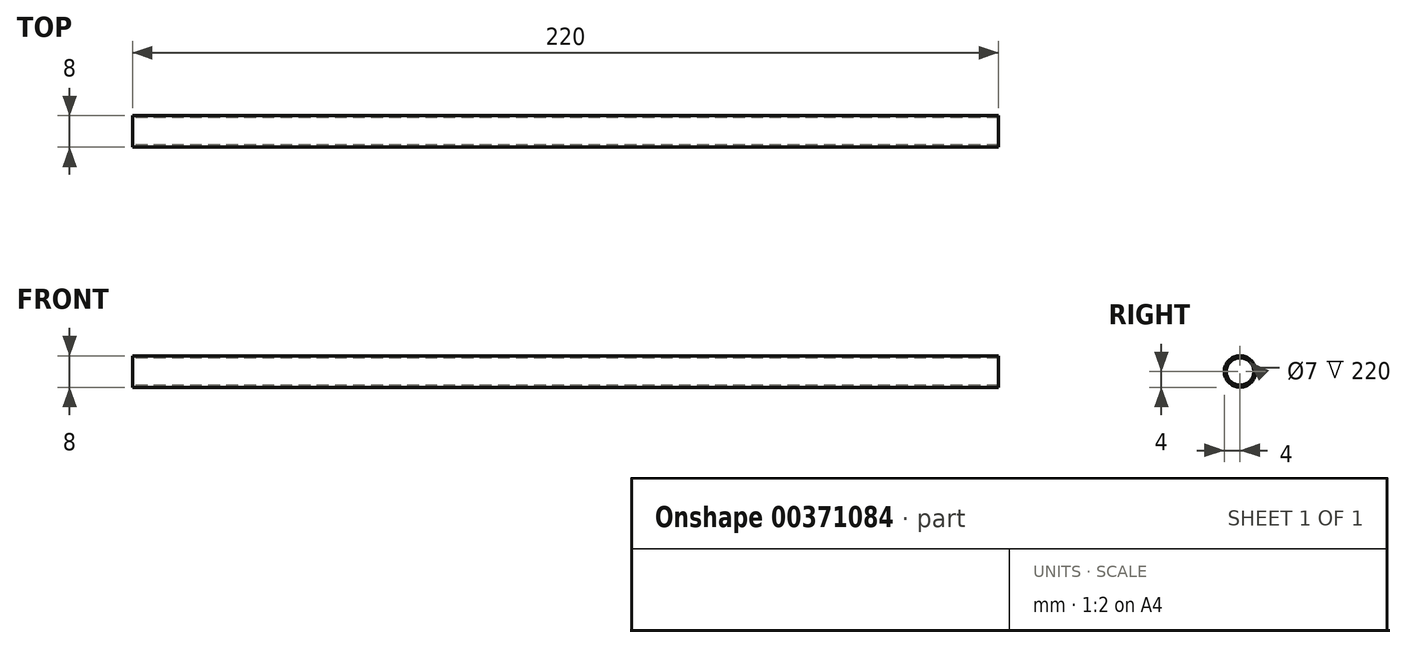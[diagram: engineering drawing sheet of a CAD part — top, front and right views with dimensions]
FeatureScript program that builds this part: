
annotation { "Feature Type Name" : "Feature", "Feature Type Description" : "" }
export const myFeature = defineFeature(function(context is Context, id is Id, definition is map)
    precondition{}
    {
        {
            var Q0;
            Q0=qCreatedBy(makeId("Right.planeOp"),FACE);
            var sketch = newSketch(context, id + "F0", { "sketchPlane" : qUnion([Q0])});
            skCircle(sketch, "E0", {"center": v(0, 0) * mm, "radius": 4 * mm});
            skCircle(sketch, "E1", {"center": v(0, 0) * mm, "radius": 3.5 * mm});
            skSolve(sketch);
        }
        {
            var Q0;
            Q0=makeQuery(id+"F0.imprint","IMPRINT",FACE,{"disambiguationData":[TD([[makeQuery(id+"F0.imprint","IMPRINT",EDGE,{"derivedFrom":sQuery(id+"F0.wireOp",EDGE,"E0")}),1.0]])]});
            extrude(context, id + "F1", {"entities" : qUnion([Q0]), "depth" : 220 * mm});
        }
    });
